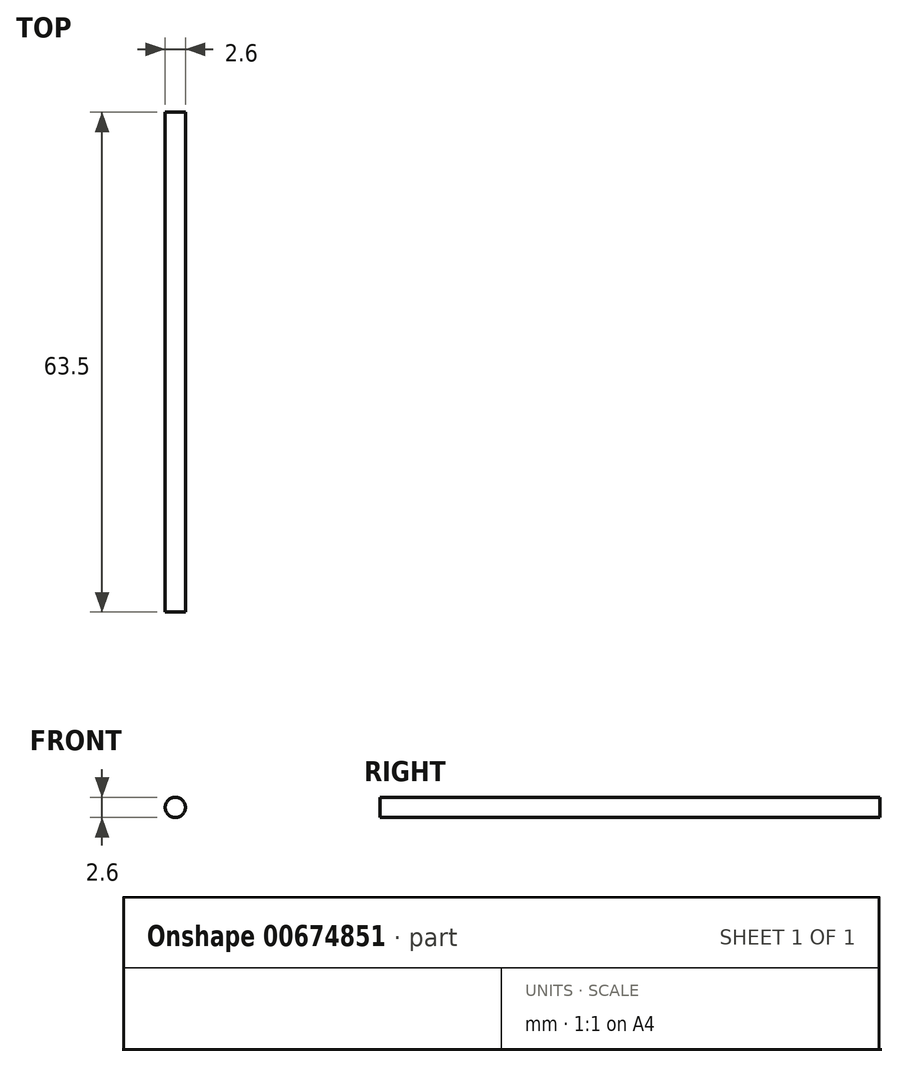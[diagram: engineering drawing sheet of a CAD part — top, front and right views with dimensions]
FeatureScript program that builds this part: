
annotation { "Feature Type Name" : "Feature", "Feature Type Description" : "" }
export const myFeature = defineFeature(function(context is Context, id is Id, definition is map)
    precondition{}
    {
        {
            var Q0;
            Q0=qCreatedBy(makeId("Front.planeOp"),FACE);
            var sketch = newSketch(context, id + "F0", { "sketchPlane" : qUnion([Q0])});
            skCircle(sketch, "E0", {"center": v(0, 0) * mm, "radius": 1.3 * mm});
            skSolve(sketch);
        }
        {
            var Q0;
            Q0 = qSketchRegion(id + "F0", true);
            extrude(context, id + "F1", {"entities" : qUnion([Q0]), "oppositeDirection" : true, "depth" : 63.5 * mm, "offsetDistance" : 25.4 * mm});
        }
    });
